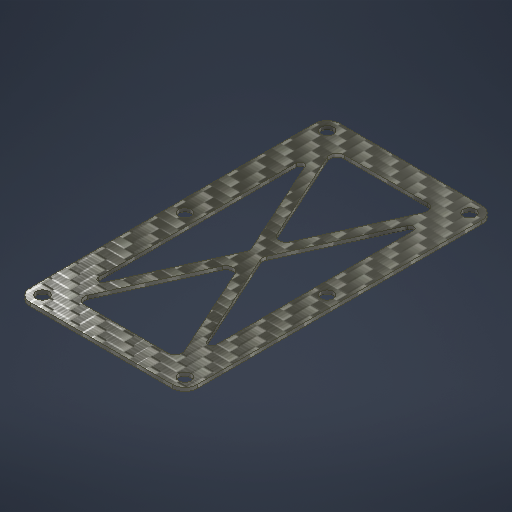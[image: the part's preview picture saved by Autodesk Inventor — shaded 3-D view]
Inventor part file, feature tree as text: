
AUTODESK INVENTOR PART (.ipt)
format: ipt  version: 2025 (Build 290162010, 162A)  size: 365,568 bytes
history: native  units: mm
features: extrude x2, fillet x2, sketch x2
ambient origin geometry x8: Origin, YZ Plane, XZ Plane, XY Plane, X Axis, Y Axis, Z Axis, Center Point
bodies: Solid1 (feature_tree)
feature tree (6):
  extrude  "Extrusion1"  Depth=80.0mm
  extrude  "Extrusion2"  Depth=3.5mm
  fillet  "Fillet1"  Radius=3.5mm
  fillet  "Fillet2"  Radius=3.5mm
  sketch  "Sketch1"  dims[d0=40.0mm d1=80.0mm]
  sketch  "Sketch2"  dims[d2=3.5mm d3=3.5mm d4=3.5mm d5=3.5mm d6=3.5mm d7=3.5mm d8=47.0mm d9=87.0mm d10=3.5mm d11=1.0mm d12=0.0mm d13=33.0mm d14=73.0mm d15=1.5mm d16=1.5mm d17=1.5mm d18=1.5mm d19=1.0mm d20=0.0mm d21=2.0mm d22=1.1mm]
